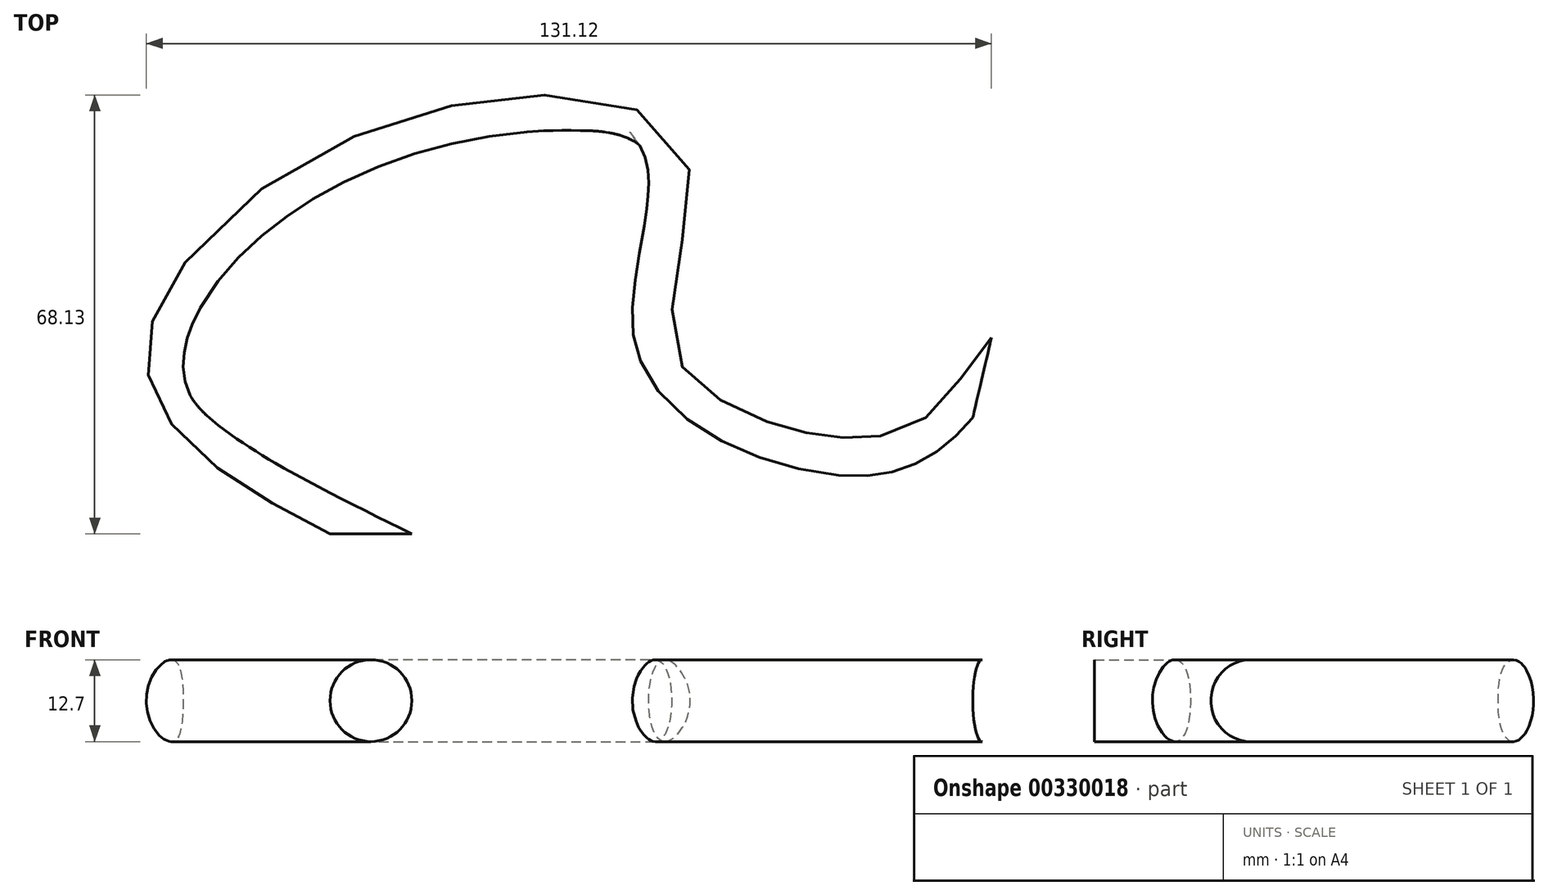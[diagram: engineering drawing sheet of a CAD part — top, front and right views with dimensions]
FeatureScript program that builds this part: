
annotation { "Feature Type Name" : "Feature", "Feature Type Description" : "" }
export const myFeature = defineFeature(function(context is Context, id is Id, definition is map)
    precondition{}
    {
        {
            var Q0;
            Q0=qCreatedBy(makeId("Front.planeOp"),FACE);
            var sketch = newSketch(context, id + "F0", { "sketchPlane" : qUnion([Q0])});
            skCircle(sketch, "E0", {"center": v(0, 0) * mm, "radius": 6.35 * mm});
            skSolve(sketch);
        }
        {
            var Q0;
            Q0=qCreatedBy(makeId("Top.planeOp"),FACE);
            var sketch = newSketch(context, id + "F1", { "sketchPlane" : qUnion([Q0])});
            skFitSpline(sketch, "E1", {"points": [v(0, 0) * mm, v(-30.83, 25.18) * mm, v(-3.53, 57.89) * mm, v(44, 59.07) * mm, v(45.42, 27.77) * mm, v(77.9, 12.7) * mm, v(94.84, 24.24) * mm], "startDerivative": vector(-248.08, 125.9) * mm, "endDerivative": vector(104.37, 124.2) * mm});
            skSolve(sketch);
        }
        {
            var Q0;
            Q0=makeQuery(id+"F0.imprint","IMPRINT",FACE,{"disambiguationData":[TD([[makeQuery(id+"F0.imprint","IMPRINT",EDGE,{"derivedFrom":sQuery(id+"F0.wireOp",EDGE,"E0")}),1.0]])]});
            var Q1;
            Q1=sQuery(id+"F1.wireOp",EDGE,"E1");
            sweep(context, id + "F2", {"profiles" : qUnion([Q0]), "path" : qUnion([Q1])});
        }
    });
